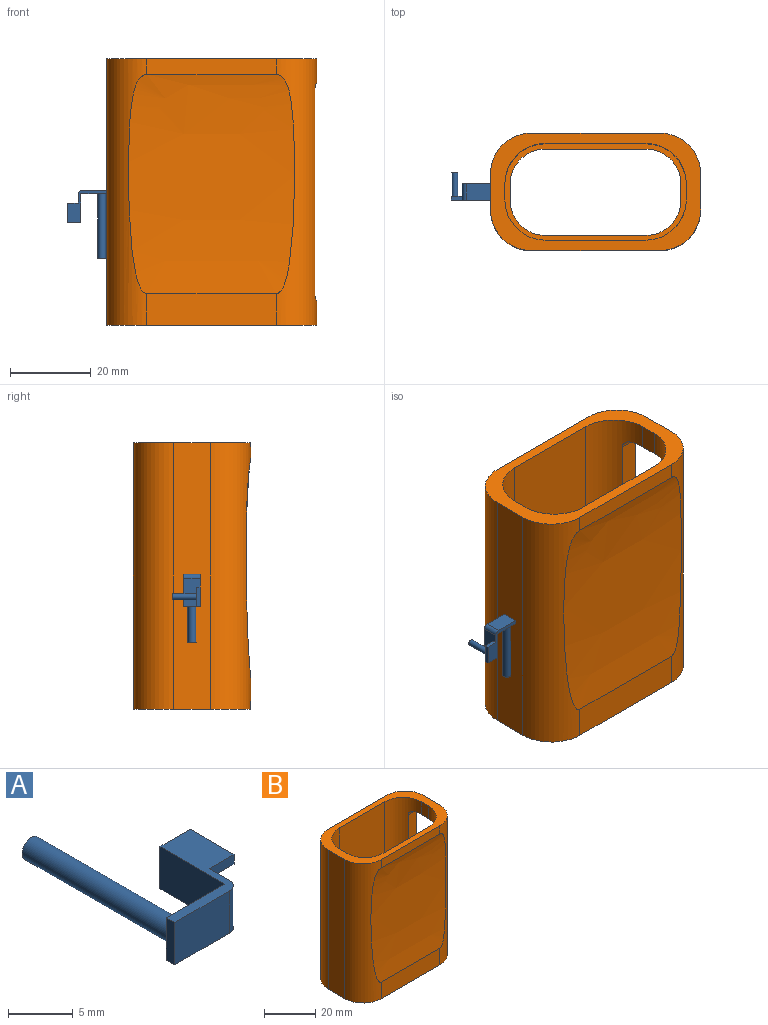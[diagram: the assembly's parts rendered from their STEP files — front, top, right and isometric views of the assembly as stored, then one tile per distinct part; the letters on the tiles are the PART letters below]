
ASSEMBLY  parts=2 mates=1
PART A: 16 faces, bbox 9.7x16.9x6.8 mm
  f0: plane 6.4x4mm, normal (0,1,0), area 22.5mm2, adj f1,f3,f4,f5,f8
  f1: cylinder r=1mm len=16mm, axis (0,1,0), area 100.5mm2, adj f0,f2
  f2: plane 2x2mm, normal (0,1,0), area 3.1mm2, adj f1
  f3: plane 9.7x8mm, normal (0,0,1), area 23.3mm2, adj f0,f4,f6,f7,f8,f9,f10,f12
  f4: plane 4x0.9mm, normal (-1,0,0), area 3.6mm2, adj f0,f3,f5,f7
  f5: plane 8x7mm, normal (0,0,-1), area 10.3mm2, adj f0,f4,f6,f7,f8,f9,f10
  f6: plane 7x4mm, normal (1,0,0), area 23.6mm2, adj f3,f5,f9,f10,f11,f12
  f7: plane 6x4mm, normal (0,-1,0), area 24mm2, adj f3,f4,f5,f10
  f8: plane 7.1x4mm, normal (-1,0,0), area 28.4mm2, adj f0,f3,f5,f9
  f9: plane 4x3.3mm, normal (0,1,0), area 4.9mm2, adj f3,f5,f6,f8,f11,f13
  f10: cylinder r=1mm len=4mm, axis (0,0,-1), area 6.3mm2, adj f3,f5,f6,f7
  f11: plane 4.8x2.7mm, normal (0,0,-1), area 11.2mm2, adj f6,f9,f12,f13,f14
  f12: plane 2.7x0.91mm, normal (0,-1,0), area 2.5mm2, adj f3,f6,f11,f13
  f13: plane 4.8x0.91mm, normal (1,0,0), area 4.4mm2, adj f3,f9,f11,f12
  f14: cylinder r=0.75mm len=5.9mm, axis (0,0,1), area 27.8mm2, adj f11,f15
  f15: plane 1.5x1.5mm, normal (0,0,-1), area 1.8mm2, adj f14
PART B: 39 faces, bbox 52.1x29.1x66.2 mm
  f0: cylinder r=10mm len=66.2mm, axis (0,0,-1), area 827mm2, adj f1,f2,f10,f19,f21,f38
  f1: plane 32.1x3.96mm, normal (0,-1,0), area 127.1mm2, adj f0,f3,f19,f38
  f2: plane 32.1x7.92mm, normal (0,-1,0), area 254.2mm2, adj f0,f3,f21,f38
  f3: cylinder r=10mm len=66.2mm, axis (0,0,-1), area 665.7mm2, adj f1,f2,f4,f6,f19,f21,f25,f26
  f4: plane 9.05x6.1mm, normal (1,0,0), area 55.2mm2, adj f3,f7,f21,f29
  f5: plane 4x3.9mm, normal (-1,0,0), area 15.6mm2, adj f13,f15,f20,f29
  f6: plane 9.05x6.1mm, normal (1,0,0), area 55.2mm2, adj f3,f7,f19,f25
  f7: cylinder r=10mm len=66.2mm, axis (0,0,-1), area 878.6mm2, adj f4,f6,f8,f19,f21,f22,f23,f24
  f8: plane 66.2x32.1mm, normal (0,1,0), area 2125.3mm2, adj f7,f9,f19,f21
  f9: cylinder r=10mm len=66.2mm, axis (0,0,-1), area 1039.9mm2, adj f8,f10,f19,f21
  f10: plane 66.2x9.05mm, normal (-1,0,0), area 599.3mm2, adj f0,f9,f19,f21
  f11: cylinder r=10mm len=64mm, axis (0,0,-1), area 1005.3mm2, adj f12,f18,f19,f20
  f12: plane 64x25mm, normal (0,-1,0), area 1600mm2, adj f11,f13,f19,f20
  f13: cylinder r=10mm len=64mm, axis (0,0,-1), area 692.8mm2, adj f5,f12,f14,f19,f20,f22,f23,f24
  f14: plane 6.1x4mm, normal (-1,0,0), area 24.4mm2, adj f13,f15,f19,f25
  f15: cylinder r=10mm len=64mm, axis (0,0,-1), area 692.8mm2, adj f5,f14,f16,f19,f20,f25,f26,f27
  f16: plane 64x25mm, normal (0,1,0), area 1600mm2, adj f15,f17,f19,f20
  f17: cylinder r=10mm len=64mm, axis (0,0,-1), area 1005.3mm2, adj f16,f18,f19,f20
  f18: plane 64x4mm, normal (1,0,0), area 256mm2, adj f11,f17,f19,f20
  f19: plane 52.1x29.05mm, normal (0,0,1), area 433.8mm2, adj f0,f1,f3,f6,f7,f8,f9,f10
  f20: plane 45x24mm, normal (0,0,1), area 151.8mm2, adj f5,f11,f12,f13,f15,f16,f17,f18
  f21: plane 52.1x29.05mm, normal (0,0,-1), area 585.6mm2, adj f0,f2,f3,f4,f7,f8,f9,f10
  f22: cylinder r=2mm len=5.15mm, axis (1,0,0), area 14.3mm2, adj f7,f13,f24,f25
  f23: cylinder r=2mm len=5.15mm, axis (1,0,0), area 14.3mm2, adj f7,f13,f24,f29
  f24: plane 50x4.75mm, normal (0,-1,0), area 237.4mm2, adj f7,f13,f22,f23
  f25: plane 11x4.19mm, normal (0,0,-1), area 40.5mm2, adj f3,f6,f7,f13,f14,f15,f22,f26
  f26: cylinder r=2mm len=5.15mm, axis (1,0,0), area 14.3mm2, adj f3,f15,f25,f27
  f27: plane 50x4.75mm, normal (0,1,0), area 237.4mm2, adj f3,f15,f26,f28
  f28: cylinder r=2mm len=5.15mm, axis (1,0,0), area 14.3mm2, adj f3,f15,f27,f29
  f29: plane 11x4.19mm, normal (0,0,1), area 40.5mm2, adj f3,f4,f5,f7,f13,f15,f23,f28
  f30: plane 25x2.2mm, normal (0,1,0), area 55mm2, adj f20,f21,f31,f37
  f31: cylinder r=8.7mm len=8.7mm, axis (0,0,-1), area 30.1mm2, adj f20,f21,f30,f32
  f32: plane 4x2.2mm, normal (1,0,0), area 8.8mm2, adj f20,f21,f31,f33
  f33: cylinder r=8.7mm len=8.7mm, axis (0,0,-1), area 30.1mm2, adj f20,f21,f32,f34
  f34: plane 25x2.2mm, normal (0,-1,0), area 55mm2, adj f20,f21,f33,f35
  f35: cylinder r=8.7mm len=8.7mm, axis (0,0,-1), area 30.1mm2, adj f20,f21,f34,f36
  f36: plane 4x2.2mm, normal (-1,0,0), area 8.8mm2, adj f20,f21,f35,f37
  f37: cylinder r=8.7mm len=8.7mm, axis (0,0,-1), area 30.1mm2, adj f20,f21,f30,f36
  f38: extruded ~54.32x41.3mm, area 2160.1mm2, adj f0,f1,f2,f3
PLACE A rot(axis=(0,-0.71,0.71),180deg) t=(-252.73,-108.29,16.38)mm
PLACE B t=(55.66,123.38,1.93)mm
MATE fastened A.f4 <-> B.f10  axis (1,0,0) through (-251.53,-108.3,32.83)mm
